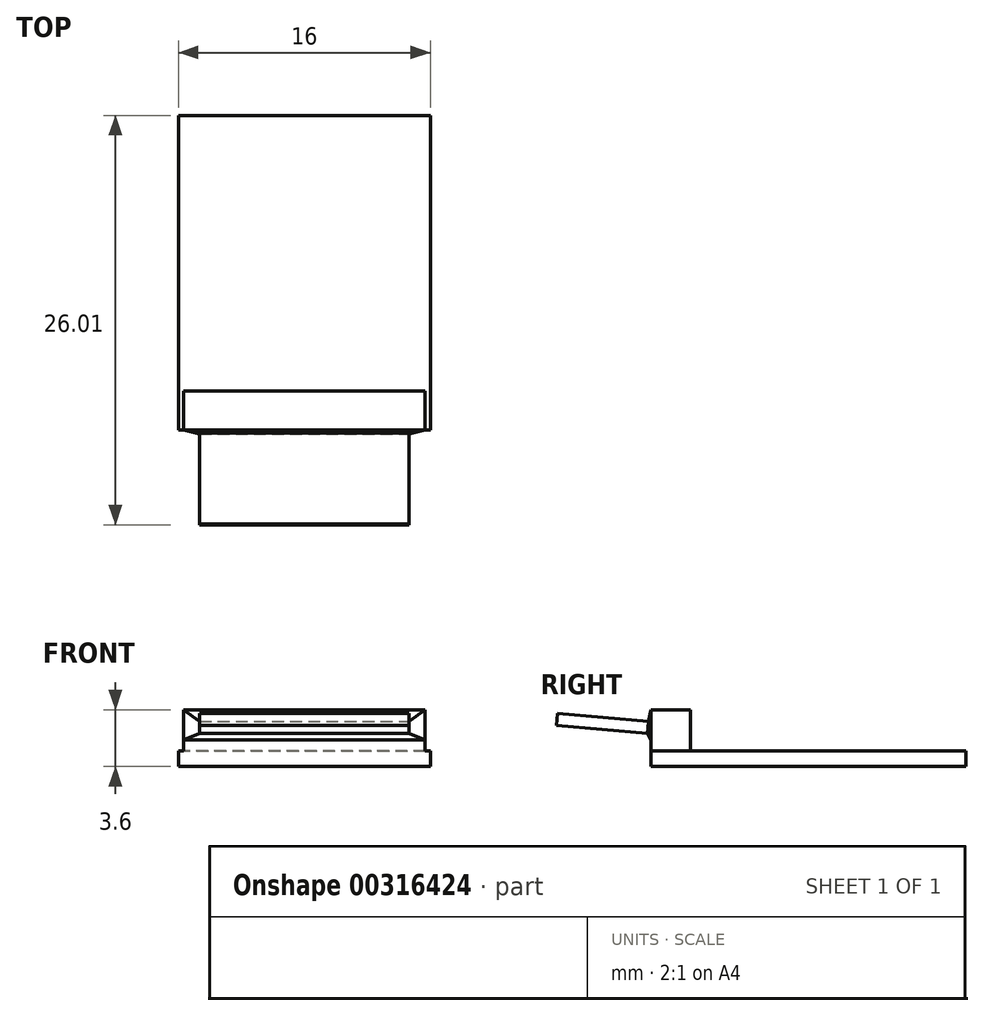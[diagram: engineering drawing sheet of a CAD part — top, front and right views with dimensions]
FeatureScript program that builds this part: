
annotation { "Feature Type Name" : "Feature", "Feature Type Description" : "" }
export const myFeature = defineFeature(function(context is Context, id is Id, definition is map)
    precondition{}
    {
        {
            var Q0;
            Q0=qCreatedBy(makeId("Top.planeOp"),FACE);
            var sketch = newSketch(context, id + "F0", { "sketchPlane" : qUnion([Q0])});
            skLineSegment(sketch, "E0.bottom", {"start": v(-8, 10) * mm, "end": v(8, 10) * mm});
            skLineSegment(sketch, "E0.top", {"start": v(-8, -10) * mm, "end": v(8, -10) * mm});
            skLineSegment(sketch, "E0.left", {"start": v(-8, 10) * mm, "end": v(-8, -10) * mm});
            skLineSegment(sketch, "E0.right", {"start": v(8, 10) * mm, "end": v(8, -10) * mm});
            skPoint(sketch, "E0.middle", {"position": v(0, 0) * mm});
            skSolve(sketch);
        }
        {
            var Q0;
            Q0 = qSketchRegion(id + "F0", true);
            extrude(context, id + "F1", {"entities" : qUnion([Q0]), "depth" : 1 * mm});
        }
        {
            var Q0;
            Q0=makeQuery(id+"F1.opExtrude","CAP_FACE",FACE,{"disambiguationData":[OSD([sQuery(id+"F0.wireOp",EDGE,"E0.bottom"),sQuery(id+"F0.wireOp",EDGE,"E0.top"),sQuery(id+"F0.wireOp",EDGE,"E0.left"),sQuery(id+"F0.wireOp",EDGE,"E0.right")])],"isStart":false});
            var sketch = newSketch(context, id + "F2", { "sketchPlane" : qUnion([Q0])});
            skLineSegment(sketch, "E1.bottom", {"start": v(7.68, -10) * mm, "end": v(-7.67, -10) * mm});
            skLineSegment(sketch, "E1.top", {"start": v(7.68, -7.5) * mm, "end": v(-7.67, -7.5) * mm});
            skLineSegment(sketch, "E1.left", {"start": v(7.68, -10) * mm, "end": v(7.68, -7.5) * mm});
            skLineSegment(sketch, "E1.right", {"start": v(-7.67, -10) * mm, "end": v(-7.67, -7.5) * mm});
            skPoint(sketch, "E1.middle", {"position": v(0, -8.75) * mm});
            skSolve(sketch);
        }
        {
            var Q0;
            Q0=makeQuery(id+"F2.imprint","IMPRINT",FACE,{"disambiguationData":[TD([[makeQuery(id+"F2.imprint","IMPRINT",EDGE,{"derivedFrom":sQuery(id+"F2.wireOp",EDGE,"E1.bottom")}),1.0]])]});
            extrude(context, id + "F3", {"entities" : qUnion([Q0]), "operationType" : NewBodyOperationType.ADD, "depth" : 2.6 * mm});
        }
        {
            var Q0;
            Q0=makeQuery(id+"F3.boolean.opBoolean","MERGE",FACE,{"derivedFrom":[makeQuery(id+"F1.opExtrude","SWEPT_FACE",FACE,{"disambiguationData":[OSD([sQuery(id+"F0.wireOp",EDGE,"E0.top")])]}),makeQuery(id+"F3.opExtrude","SWEPT_FACE",FACE,{"disambiguationData":[OSD([sQuery(id+"F2.wireOp",EDGE,"E1.bottom")])]})]});
            var sketch = newSketch(context, id + "F4", { "sketchPlane" : qUnion([Q0])});
            skLineSegment(sketch, "E2", {"start": v(-7.67, 1.7) * mm, "end": v(7.67, 1.7) * mm});
            skSolve(sketch);
        }
        {
            var Q0;
            Q0=makeQuery(id+"F3.opExtrude","CAP_EDGE",EDGE,{"disambiguationData":[OSD([sQuery(id+"F2.wireOp",EDGE,"E1.bottom")])],"isStart":false});
            var Q1;
            {var subQ0=sQuery(id+"F4.wireOp",EDGE,"E2");Q1=makeQuery(id+"F4.imprint","IMPRINT",FACE,{"disambiguationData":[TD([[makeQuery(id+"F4.imprint","IMPRINT",EDGE,{"derivedFrom":subQ0}),1.0]])]});}
            cPlane(context, id + "F5", {"entities" : qUnion([Q0, Q1]), "cplaneType" : CPlaneType.LINE_ANGLE, "offset" : 25 * mm, "angle" : 5 * degree, "oppositeDirection" : true, "width" : 150 * mm, "height" : 150 * mm});
        }
        {
            var Q0;
            Q0=qCreatedBy(id+"F5.planeOp",FACE);
            cPlane(context, id + "F6", {"entities" : qUnion([Q0]), "cplaneType" : CPlaneType.OFFSET, "offset" : 0.1 * mm, "oppositeDirection" : true, "width" : 150 * mm, "height" : 150 * mm});
        }
        {
            var Q0;
            Q0=qCreatedBy(id+"F6.planeOp",FACE);
            var sketch = newSketch(context, id + "F7", { "sketchPlane" : qUnion([Q0])});
            skLineSegment(sketch, "E3.bottom", {"start": v(6.65, 1.96) * mm, "end": v(-6.65, 1.96) * mm});
            skLineSegment(sketch, "E3.top", {"start": v(6.65, 1.21) * mm, "end": v(-6.65, 1.21) * mm});
            skLineSegment(sketch, "E3.left", {"start": v(6.65, 1.96) * mm, "end": v(6.65, 1.21) * mm});
            skLineSegment(sketch, "E3.right", {"start": v(-6.65, 1.96) * mm, "end": v(-6.65, 1.21) * mm});
            skPoint(sketch, "E3.middle", {"position": v(0, 1.59) * mm});
            skSolve(sketch);
        }
        {
            var Q0;
            Q0=makeQuery(id+"F7.imprint","IMPRINT",FACE,{"disambiguationData":[TD([[makeQuery(id+"F7.imprint","IMPRINT",EDGE,{"derivedFrom":sQuery(id+"F7.wireOp",EDGE,"E3.bottom")}),1.0]])]});
            extrude(context, id + "F8", {"entities" : qUnion([Q0]), "oppositeDirection" : true, "depth" : 5.8 * mm});
        }
        {
            var Q2;
            {var subQ0=sQuery(id+"F4.wireOp",EDGE,"E2");Q2=makeQuery(id+"F4.imprint","IMPRINT",FACE,{"disambiguationData":[TD([[makeQuery(id+"F4.imprint","IMPRINT",EDGE,{"derivedFrom":subQ0}),1.0]])]});}
            var Q3;
            Q3=makeQuery(id+"F8.opExtrude","CAP_FACE",FACE,{"disambiguationData":[OSD([sQuery(id+"F7.wireOp",EDGE,"E3.bottom"),sQuery(id+"F7.wireOp",EDGE,"E3.top"),sQuery(id+"F7.wireOp",EDGE,"E3.left"),sQuery(id+"F7.wireOp",EDGE,"E3.right")])],"isStart":true});
            loft(context, id + "F9", {"operationType" : NewBodyOperationType.ADD, "sheetProfilesArray" : [{ "sheetProfileEntities" : qUnion([Q2]) }, { "sheetProfileEntities" : qUnion([Q3]) }]});
        }
    });
